# Revit family: ASL_64_Series_al_door_100mm_Mullion
name_source: partatom
category: Detail Items
revit_build: Autodesk Revit 2018 (Build: 20170223_1515(x64)
units: mm (PartAtom-declared; Revit-internal decimal feet)

## family parameters
Rotate with component = No
Section Shape = Not Defined
Shared = Yes

## types (5) — shared parameters
Door Mullion Post_ASL_544 = Yes
Glazing_2 = Yes
Manufacturer = Aluminate Solutions Limited
Technical Info = www.aluminate.nz

## per-type parameters (varying)
| type | ASL Hinge | ASL_Hinge_Door_100 | ASL_Hinge_Door_100 Option | Door Stop_50 | Flush Infill | Glazing | Type Comments |
| Double Action ASL Hinge Stile Door Suite 100mm | No | Yes | ASL_Door Suite_Stile_100mm : Hinge Stile Hinge Door 100mm | No | Yes | No | ASL 64 Series Mullion With Double Action ASL 100mm Hinge Stile Door Suite |
| Single Action ASL Lockset Stile Door Suite 100mm | No | Yes | ASL_Door Suite_Stile_100mm : Lockset Stile Hinge Door 100mm | Yes | No | No | ASL 64 Series Jamb 2 With Single Action ASL 100mm Lockset Stile Door Suite |
| Double Action ASL Lockset Stile Door Suite 100mm | No | Yes | ASL_Door Suite_Stile_100mm : Lockset Stile Double Action Hinge, Pviot and Sliding Door 100mm | No | Yes | No | ASL 64 Series Mullion With Double Action ASL 100mm Lockset Stile Door Suite |
| Single Action ASL Hinge Stile Door Suite 100mm | Yes | Yes | ASL_Door Suite_Stile_100mm : Hinge Stile Hinge Door 100mm | Yes | No | No | ASL 64 Series Mullion With Single Action ASL 100mm Hinge Stile Door Suite |
| Glazing | No | No | ASL_Door Suite_Stile_100mm : Hinge Stile Hinge Door 100mm | No | No | Yes | ASL 64 Series Mullion With Glazing |

## geometry (parser evidence)
native form markers: Sweep x12
no freeform markers — native parametric forms only
